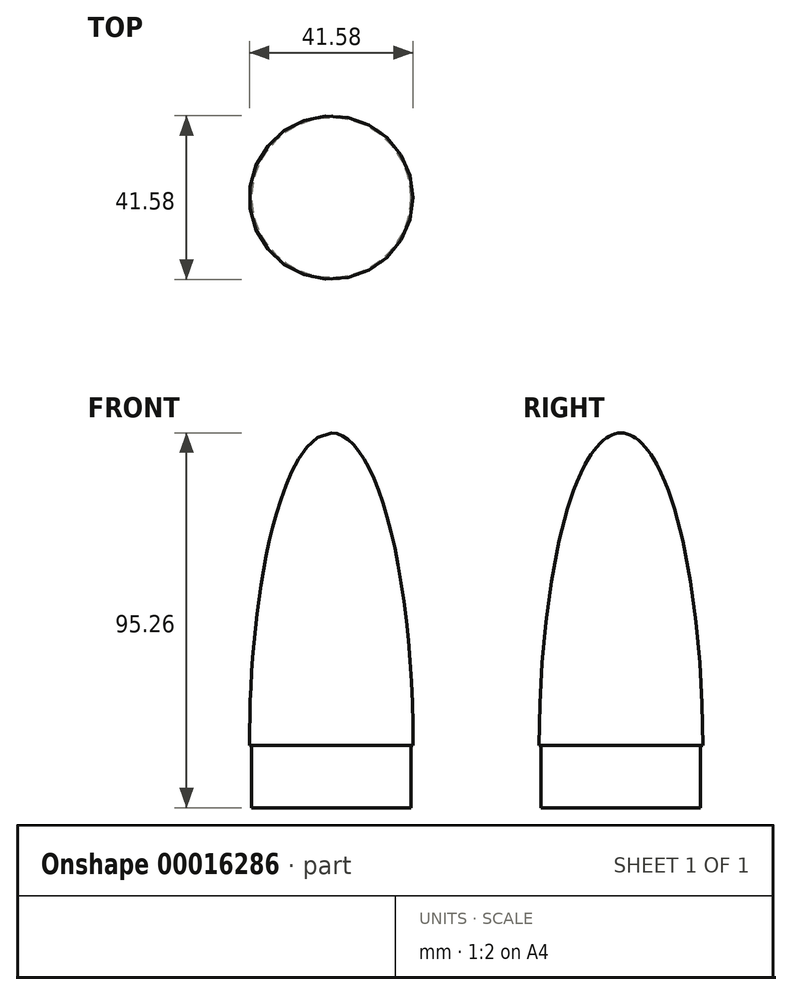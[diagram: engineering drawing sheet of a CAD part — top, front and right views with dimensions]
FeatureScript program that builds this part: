
annotation { "Feature Type Name" : "Feature", "Feature Type Description" : "" }
export const myFeature = defineFeature(function(context is Context, id is Id, definition is map)
    precondition{}
    {
        {
            var Q0;
            Q0=qCreatedBy(makeId("Front.planeOp"),FACE);
            var sketch = newSketch(context, id + "F0", { "sketchPlane" : qUnion([Q0])});
            skLineSegment(sketch, "E0", {"start": v(0, 0) * mm, "end": v(0, 79.37) * mm});
            skLineSegment(sketch, "E1", {"start": v(0, 0) * mm, "end": v(20.79, 0) * mm});
            skLineSegment(sketch, "E2", {"start": v(0, 0) * mm, "end": v(0, -15.87) * mm});
            skLineSegment(sketch, "E3", {"start": v(0, -15.88) * mm, "end": v(20.26, -15.88) * mm});
            skLineSegment(sketch, "E4", {"start": v(20.26, -15.88) * mm, "end": v(20.26, 0) * mm});
            skEllipticalArc(sketch, "E5", {});
            const initialGuessF0  = {"E5": [0, 0, 0, 1, 0.079375, 0.020789900000000004, 4.71238898038469, 0]};
            skSetInitialGuess(sketch, initialGuessF0);
            skSolve(sketch);
        }
        {
            var Q0;
            {var subQ3=sQuery(id+"F0.wireOp",EDGE,"E0");Q0=makeQuery(id+"F0.imprint","IMPRINT",FACE,{"disambiguationData":[TD([[makeQuery(id+"F0.imprint","IMPRINT",EDGE,{"derivedFrom":subQ3}),-1.0]])]});}
            var Q1;
            {var subQ1=sQuery(id+"F0.wireOp",EDGE,"E2");Q1=makeQuery(id+"F0.imprint","IMPRINT",FACE,{"disambiguationData":[TD([[makeQuery(id+"F0.imprint","IMPRINT",EDGE,{"derivedFrom":subQ1}),1.0]])]});}
            var Q2;
            Q2=sQuery(id+"F0.wireOp",EDGE,"E0");
            revolve(context, id + "F1", {"entities" : qUnion([Q0, Q1]), "axis" : qUnion([Q2]), "revolveType" : RevolveType.FULL});
        }
    });
